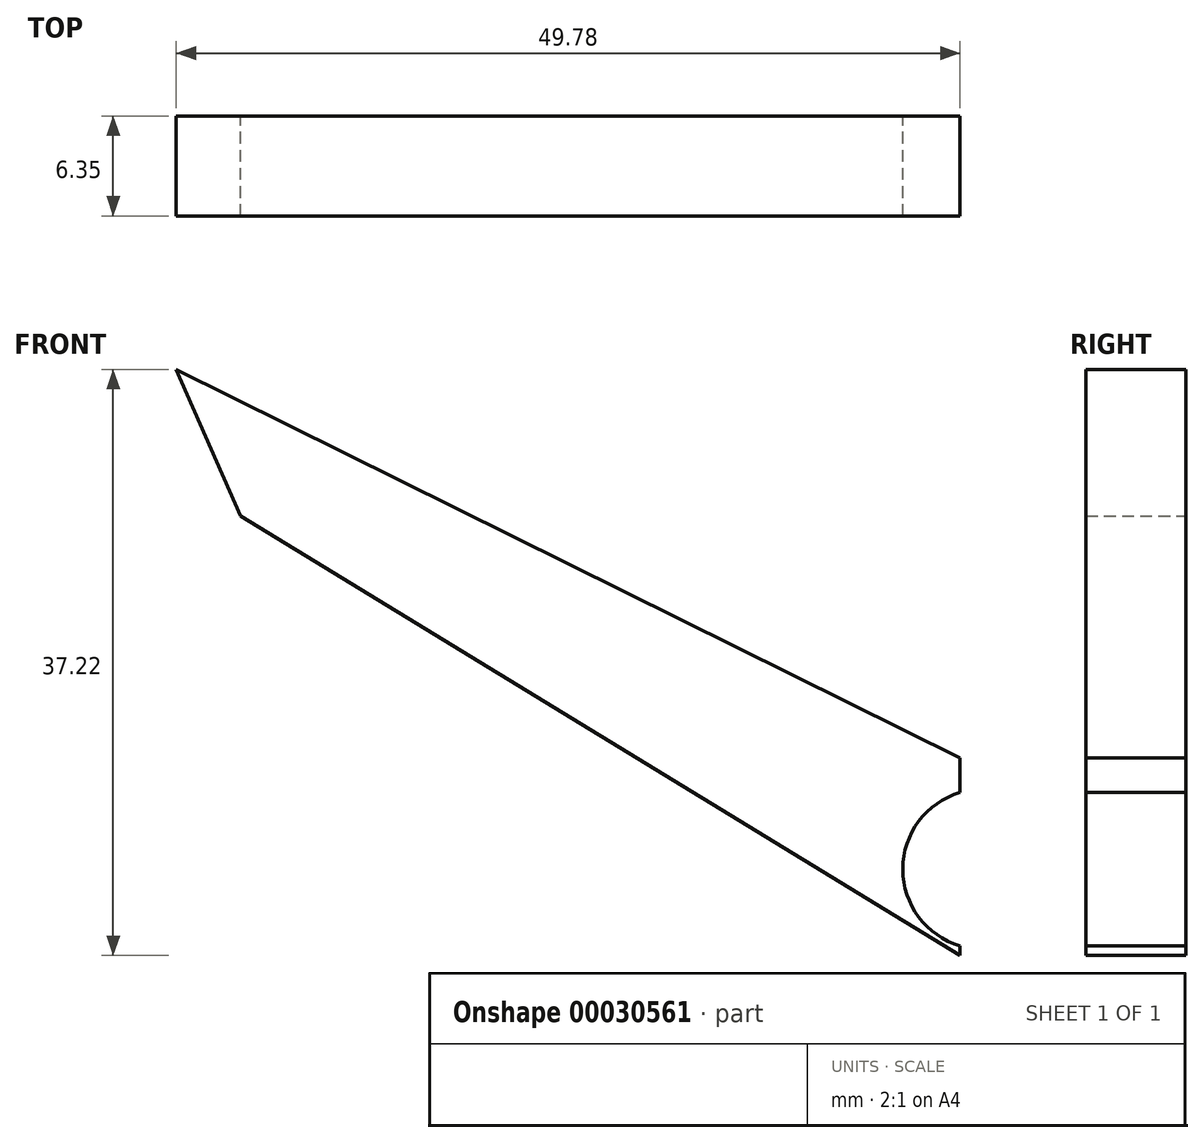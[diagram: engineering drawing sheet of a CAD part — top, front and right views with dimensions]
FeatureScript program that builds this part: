
annotation { "Feature Type Name" : "Feature", "Feature Type Description" : "" }
export const myFeature = defineFeature(function(context is Context, id is Id, definition is map)
    precondition{}
    {
        {
            var Q0;
            Q0=qCreatedBy(makeId("Front.planeOp"),FACE);
            var sketch = newSketch(context, id + "F0", { "sketchPlane" : qUnion([Q0])});
            skLineSegment(sketch, "E0", {"start": v(-4.34, -8.34) * mm, "end": v(-51.47, 20.44) * mm});
            skLineSegment(sketch, "E1", {"start": v(-55.54, 29.75) * mm, "end": v(-4.34, 4.36) * mm});
            skLineSegment(sketch, "E2", {"start": v(-4.34, 4.36) * mm, "end": v(-4.34, -8.34) * mm});
            skPoint(sketch, "E3.orphan", {"position": v(-6.68, -4.04) * mm});
            skLineSegment(sketch, "E4", {"start": v(-5.76, 6.16) * mm, "end": v(-5.76, -9.18) * mm});
            skLineSegment(sketch, "E5", {"start": v(-4.34, 4.36) * mm, "end": v(-4.34, 3.1) * mm});
            skLineSegment(sketch, "E6", {"start": v(-4.34, -8.34) * mm, "end": v(-4.34, -7.07) * mm});
            skArc(sketch, "E7", {"start": v(-4.34, 3.1) * mm, "mid": v(-9.4, -1.99) * mm, "end": v(-4.34, -7.07) * mm});
            skLineSegment(sketch, "E8", {"start": v(-55.54, 29.75) * mm, "end": v(-51.47, 20.44) * mm});
            skSolve(sketch);
        }
        {
            var Q0;
            {var subQ3=sQuery(id+"F0.wireOp",EDGE,"E6");Q0=makeQuery(id+"F0.imprint","IMPRINT",FACE,{"disambiguationData":[TD([[makeQuery(id+"F0.imprint","IMPRINT",EDGE,{"derivedFrom":subQ3}),1.0]])]});}
            var Q1;
            {var subQ3=sQuery(id+"F0.wireOp",EDGE,"E5");Q1=makeQuery(id+"F0.imprint","IMPRINT",FACE,{"disambiguationData":[TD([[makeQuery(id+"F0.imprint","IMPRINT",EDGE,{"derivedFrom":subQ3}),-1.0]])]});}
            var Q2;
            {var subQ0=sQuery(id+"F0.wireOp",EDGE,"e6664576-3001-43b4-84cc-5fbf448b5242");Q2=makeQuery(id+"F0.imprint","IMPRINT",FACE,{"disambiguationData":[TD([[makeQuery(id+"F0.imprint","IMPRINT",EDGE,{"derivedFrom":subQ0}),-1.0]])]});}
            var Q3;
            {var subQ0=sQuery(id+"F0.wireOp",EDGE,"E8");Q3=makeQuery(id+"F0.imprint","IMPRINT",FACE,{"disambiguationData":[TD([[makeQuery(id+"F0.imprint","IMPRINT",EDGE,{"derivedFrom":subQ0}),1.0]])]});}
            extrude(context, id + "F1", {"entities" : qUnion([Q0, Q1, Q2, Q3]), "depth" : 6.35 * mm});
        }
    });
